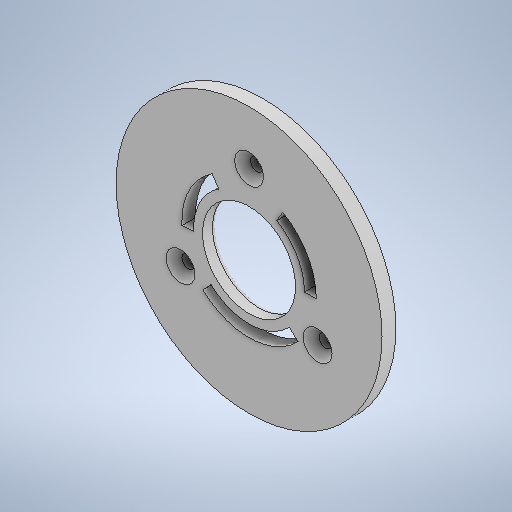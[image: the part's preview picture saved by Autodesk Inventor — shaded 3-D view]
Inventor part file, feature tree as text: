
AUTODESK INVENTOR PART (.ipt)
format: ipt  version: 2025 (Build 290162000, 162)  size: 332,800 bytes
history: native  units: mm
features: sketch x3, extrude x3, fillet x1, chamfer x1
ambient origin geometry x8: Origin, YZ Plane, XZ Plane, XY Plane, X Axis, Y Axis, Z Axis, Center Point
bodies: 实体1 (feature_tree)
feature tree (8):
  sketch  "草图1"  dims[d0=67.2mm d1=40.0mm]
  extrude  "拉伸1"  Depth=40.0mm
  extrude  "拉伸2"  Depth=30.0mm TaperAngle=360.0deg
  extrude  "拉伸3"  Depth=3.5mm TaperAngle=0.0deg
  fillet  "圆角1"  Radius=43.3mm
  chamfer  "倒角1"  Distance=10.3mm
  sketch  "草图 - 环形阵列1"  dims[d2=3.3mm d3=30.0mm d5=360.0deg]
  sketch  "草图 - 环形阵列2"  dims[d7=23.5mm d8=3.5mm d9=0.0mm d10=43.3mm d11=10.3mm d12=160.0mm d14=360.0deg d16=2.0mm d17=0.0mm d18=14.0mm d19=3.0mm d20=45.0deg d21=60.0deg d22=45.0deg d23=5.0mm d24=0.0mm d25=1.0mm d26=2.0mm d27=2.0mm d28=45.0deg]
